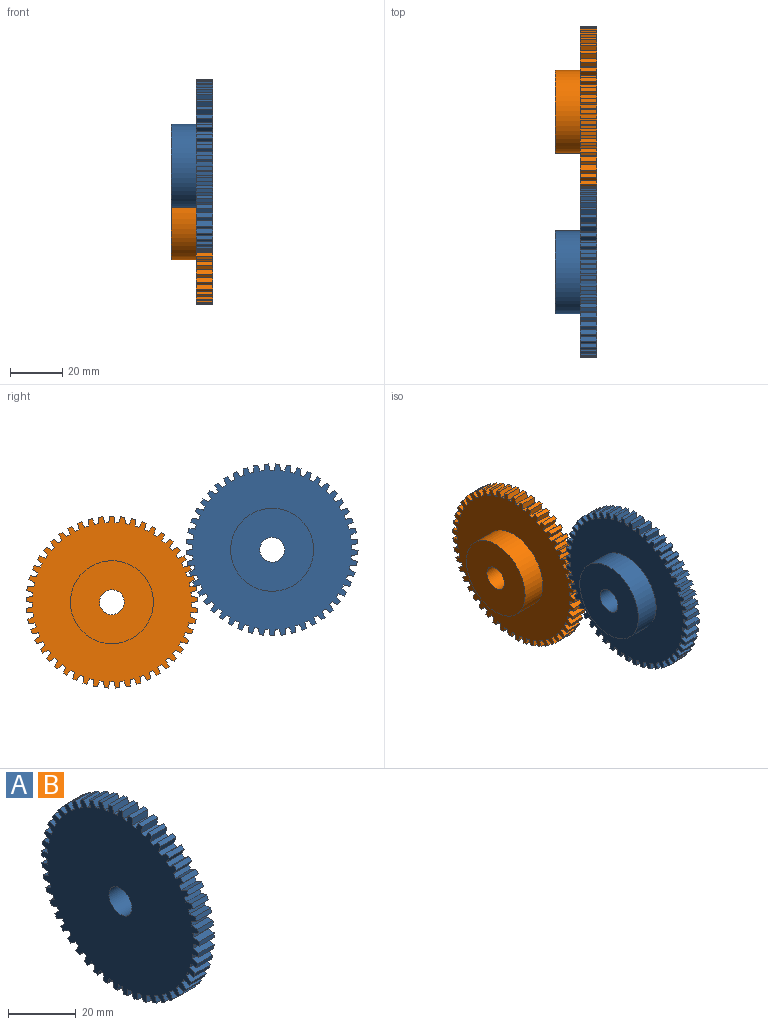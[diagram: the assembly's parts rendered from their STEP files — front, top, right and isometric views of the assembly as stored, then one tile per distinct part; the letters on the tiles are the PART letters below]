
ASSEMBLY  parts=2 mates=1
PART A: 201 faces, bbox 15.9x65.7x65.7 mm
  f0: cylinder r=30.48mm len=6.35mm, axis (-1,0,0), area 9.7mm2, adj f50,f51,f131,f134
  f1: cylinder r=30.48mm len=6.35mm, axis (-1,0,0), area 9.7mm2, adj f50,f51,f133,f137
  f2: cylinder r=30.48mm len=6.35mm, axis (-1,0,0), area 9.7mm2, adj f50,f51,f136,f140
  f3: cylinder r=30.48mm len=6.35mm, axis (-1,0,0), area 9.7mm2, adj f50,f51,f139,f143
  f4: cylinder r=30.48mm len=6.35mm, axis (-1,0,0), area 9.7mm2, adj f50,f51,f142,f146
  f5: cylinder r=30.48mm len=6.35mm, axis (-1,0,0), area 9.7mm2, adj f50,f51,f145,f149
  f6: cylinder r=30.48mm len=6.35mm, axis (-1,0,0), area 9.7mm2, adj f50,f51,f148,f152
  f7: cylinder r=30.48mm len=6.35mm, axis (-1,0,0), area 9.7mm2, adj f50,f51,f151,f155
  f8: cylinder r=30.48mm len=6.35mm, axis (-1,0,0), area 9.7mm2, adj f50,f51,f154,f158
  f9: cylinder r=30.48mm len=6.35mm, axis (-1,0,0), area 9.7mm2, adj f50,f51,f157,f161
  f10: cylinder r=30.48mm len=6.35mm, axis (-1,0,0), area 9.7mm2, adj f50,f51,f160,f164
  f11: cylinder r=30.48mm len=6.35mm, axis (-1,0,0), area 9.7mm2, adj f50,f51,f163,f167
  f12: cylinder r=30.48mm len=6.35mm, axis (-1,0,0), area 9.7mm2, adj f50,f51,f166,f170
  f13: cylinder r=30.48mm len=6.35mm, axis (-1,0,0), area 9.7mm2, adj f50,f51,f169,f173
  f14: cylinder r=30.48mm len=6.35mm, axis (-1,0,0), area 9.7mm2, adj f50,f51,f172,f176
  f15: cylinder r=30.48mm len=6.35mm, axis (-1,0,0), area 9.7mm2, adj f50,f51,f175,f179
  f16: cylinder r=30.48mm len=6.35mm, axis (-1,0,0), area 9.7mm2, adj f50,f51,f178,f182
  f17: cylinder r=30.48mm len=6.35mm, axis (-1,0,0), area 9.7mm2, adj f50,f51,f181,f185
  f18: cylinder r=30.48mm len=6.35mm, axis (-1,0,0), area 9.7mm2, adj f50,f51,f184,f188
  f19: cylinder r=30.48mm len=6.35mm, axis (-1,0,0), area 9.7mm2, adj f50,f51,f187,f191
  f20: cylinder r=30.48mm len=6.35mm, axis (-1,0,0), area 9.7mm2, adj f50,f51,f190,f194
  f21: cylinder r=30.48mm len=6.35mm, axis (-1,0,0), area 9.7mm2, adj f50,f51,f193,f197
  f22: cylinder r=30.48mm len=6.35mm, axis (-1,0,0), area 9.7mm2, adj f50,f51,f196,f198
  f23: cylinder r=30.48mm len=6.35mm, axis (-1,0,0), area 9.7mm2, adj f50,f51,f59,f200
  f24: cylinder r=30.48mm len=6.35mm, axis (-1,0,0), area 9.7mm2, adj f50,f51,f58,f62
  f25: cylinder r=30.48mm len=6.35mm, axis (-1,0,0), area 9.7mm2, adj f50,f51,f61,f65
  f26: cylinder r=30.48mm len=6.35mm, axis (-1,0,0), area 9.7mm2, adj f50,f51,f64,f68
  f27: cylinder r=30.48mm len=6.35mm, axis (-1,0,0), area 9.7mm2, adj f50,f51,f67,f71
  f28: cylinder r=30.48mm len=6.35mm, axis (-1,0,0), area 9.7mm2, adj f50,f51,f70,f74
  f29: cylinder r=30.48mm len=6.35mm, axis (-1,0,0), area 9.7mm2, adj f50,f51,f73,f77
  f30: cylinder r=30.48mm len=6.35mm, axis (-1,0,0), area 9.7mm2, adj f50,f51,f76,f80
  f31: cylinder r=30.48mm len=6.35mm, axis (-1,0,0), area 9.7mm2, adj f50,f51,f79,f83
  f32: cylinder r=30.48mm len=6.35mm, axis (-1,0,0), area 9.7mm2, adj f50,f51,f82,f86
  f33: cylinder r=30.48mm len=6.35mm, axis (-1,0,0), area 9.7mm2, adj f50,f51,f85,f89
  f34: cylinder r=30.48mm len=6.35mm, axis (-1,0,0), area 9.7mm2, adj f50,f51,f88,f92
  f35: cylinder r=30.48mm len=6.35mm, axis (-1,0,0), area 9.7mm2, adj f50,f51,f91,f95
  f36: cylinder r=30.48mm len=6.35mm, axis (-1,0,0), area 9.7mm2, adj f50,f51,f94,f98
  f37: cylinder r=30.48mm len=6.35mm, axis (-1,0,0), area 9.7mm2, adj f50,f51,f97,f101
  f38: cylinder r=30.48mm len=6.35mm, axis (-1,0,0), area 9.7mm2, adj f50,f51,f100,f104
  f39: cylinder r=30.48mm len=6.35mm, axis (-1,0,0), area 9.7mm2, adj f50,f51,f103,f107
  f40: cylinder r=30.48mm len=6.35mm, axis (-1,0,0), area 9.7mm2, adj f50,f51,f106,f110
  f41: cylinder r=30.48mm len=6.35mm, axis (-1,0,0), area 9.7mm2, adj f50,f51,f109,f113
  f42: cylinder r=30.48mm len=6.35mm, axis (-1,0,0), area 9.7mm2, adj f50,f51,f112,f116
  f43: cylinder r=30.48mm len=6.35mm, axis (-1,0,0), area 9.7mm2, adj f50,f51,f115,f119
  f44: cylinder r=30.48mm len=6.35mm, axis (-1,0,0), area 9.7mm2, adj f50,f51,f118,f122
  f45: cylinder r=30.48mm len=6.35mm, axis (-1,0,0), area 9.7mm2, adj f50,f51,f121,f125
  f46: cylinder r=30.48mm len=6.35mm, axis (-1,0,0), area 9.7mm2, adj f50,f51,f124,f128
  f47: cylinder r=30.48mm len=6.35mm, axis (-1,0,0), area 9.7mm2, adj f50,f51,f54,f127
  f48: cylinder r=30.48mm len=6.35mm, axis (-1,0,0), area 9.7mm2, adj f50,f51,f56,f130
  f49: cylinder r=15.88mm len=31.75mm, axis (-1,0,0), area 956.4mm2, adj f50,f53
  f50: plane 65.72x65.69mm, normal (1,0,0), area 2358mm2, adj f0,f1,f2,f3,f4,f5,f6,f7
  f51: plane 65.72x65.69mm, normal (-1,0,0), area 3078.4mm2, adj f0,f1,f2,f3,f4,f5,f6,f7
  f52: cylinder r=4.76mm len=15.94mm, axis (-1,0,0), area 476.9mm2, adj f51,f53
  f53: plane 31.75x31.75mm, normal (1,0,0), area 720.5mm2, adj f49,f52
  f54: plane 6.35x2.4mm, normal (0,-0.99,0.16), area 15.4mm2, adj f47,f50,f51,f55
  f55: plane 6.35x1.59mm, normal (0,0,1), area 10.1mm2, adj f50,f51,f54,f56
  f56: plane 6.35x2.4mm, normal (0,0.99,0.16), area 15.4mm2, adj f48,f50,f51,f55
  f57: plane 6.35x1.58mm, normal (0,-0.06,-1), area 10.1mm2, adj f50,f51,f58,f59
  f58: plane 6.35x2.42mm, normal (0,-0.99,-0.1), area 15.4mm2, adj f24,f50,f51,f57
  f59: plane 6.35x2.36mm, normal (0,0.97,-0.23), area 15.4mm2, adj f23,f50,f51,f57
  f60: plane 6.35x1.56mm, normal (0,-0.19,-0.98), area 10.1mm2, adj f50,f51,f61,f62
  f61: plane 6.35x2.43mm, normal (0,-1,0.03), area 15.4mm2, adj f25,f50,f51,f60
  f62: plane 6.35x2.28mm, normal (0,0.94,-0.35), area 15.4mm2, adj f24,f50,f51,f60
  f63: plane 6.35x1.51mm, normal (0,-0.32,-0.95), area 10.1mm2, adj f50,f51,f64,f65
  f64: plane 6.35x2.4mm, normal (0,-0.99,0.16), area 15.4mm2, adj f26,f50,f51,f63
  f65: plane 6.35x2.15mm, normal (0,0.88,-0.47), area 15.4mm2, adj f25,f50,f51,f63
  f66: plane 6.35x1.43mm, normal (0,-0.43,-0.9), area 10.1mm2, adj f50,f51,f67,f68
  f67: plane 6.35x2.33mm, normal (0,-0.96,0.28), area 15.4mm2, adj f27,f50,f51,f66
  f68: plane 6.35x1.99mm, normal (0,0.82,-0.58), area 15.4mm2, adj f26,f50,f51,f66
  f69: plane 6.35x1.33mm, normal (0,-0.55,-0.84), area 10.1mm2, adj f50,f51,f70,f71
  f70: plane 6.35x2.22mm, normal (0,-0.92,0.4), area 15.4mm2, adj f28,f50,f51,f69
  f71: plane 6.35x1.79mm, normal (0,0.74,-0.68), area 15.4mm2, adj f27,f50,f51,f69
  f72: plane 6.35x1.21mm, normal (0,-0.65,-0.76), area 10.1mm2, adj f50,f51,f73,f74
  f73: plane 6.35x2.08mm, normal (0,-0.86,0.52), area 15.4mm2, adj f29,f50,f51,f72
  f74: plane 6.35x1.85mm, normal (0,0.65,-0.76), area 15.4mm2, adj f28,f50,f51,f72
  f75: plane 6.35x1.18mm, normal (0,-0.74,-0.67), area 10.1mm2, adj f50,f51,f76,f77
  f76: plane 6.35x1.9mm, normal (0,-0.78,0.62), area 15.4mm2, adj f30,f50,f51,f75
  f77: plane 6.35x2.04mm, normal (0,0.54,-0.84), area 15.4mm2, adj f29,f50,f51,f75
  f78: plane 6.35x1.3mm, normal (0,-0.82,-0.57), area 10.1mm2, adj f50,f51,f79,f80
  f79: plane 6.35x1.74mm, normal (0,-0.7,0.72), area 15.4mm2, adj f31,f50,f51,f78
  f80: plane 6.35x2.19mm, normal (0,0.43,-0.9), area 15.4mm2, adj f30,f50,f51,f78
  f81: plane 6.35x1.41mm, normal (0,-0.89,-0.46), area 10.1mm2, adj f50,f51,f82,f83
  f82: plane 6.35x1.94mm, normal (0,-0.6,0.8), area 15.4mm2, adj f32,f50,f51,f81
  f83: plane 6.35x2.31mm, normal (0,0.31,-0.95), area 15.4mm2, adj f31,f50,f51,f81
  f84: plane 6.35x1.49mm, normal (0,-0.94,-0.35), area 10.1mm2, adj f50,f51,f85,f86
  f85: plane 6.35x2.11mm, normal (0,-0.49,0.87), area 15.4mm2, adj f33,f50,f51,f84
  f86: plane 6.35x2.38mm, normal (0,0.19,-0.98), area 15.4mm2, adj f32,f50,f51,f84
  f87: plane 6.35x1.55mm, normal (0,-0.97,-0.22), area 10.1mm2, adj f50,f51,f88,f89
  f88: plane 6.35x2.25mm, normal (0,-0.38,0.93), area 15.4mm2, adj f34,f50,f51,f87
  f89: plane 6.35x2.42mm, normal (0,0.06,-1), area 15.4mm2, adj f33,f50,f51,f87
  f90: plane 6.35x1.58mm, normal (0,-1,-0.1), area 10.1mm2, adj f50,f51,f91,f92
  f91: plane 6.35x2.35mm, normal (0,-0.26,0.97), area 15.4mm2, adj f35,f50,f51,f90
  f92: plane 6.35x2.42mm, normal (0,-0.07,-1), area 15.4mm2, adj f34,f50,f51,f90
  f93: plane 6.35x1.59mm, normal (0,-1,0.03), area 10.1mm2, adj f50,f51,f94,f95
  f94: plane 6.35x2.41mm, normal (0,-0.13,0.99), area 15.4mm2, adj f36,f50,f51,f93
  f95: plane 6.35x2.38mm, normal (0,-0.2,-0.98), area 15.4mm2, adj f35,f50,f51,f93
  f96: plane 6.35x1.57mm, normal (0,-0.99,0.16), area 10.1mm2, adj f50,f51,f97,f98
  f97: plane 6.35x2.43mm, normal (0,0,1), area 15.4mm2, adj f37,f50,f51,f96
  f98: plane 6.35x2.3mm, normal (0,-0.32,-0.95), area 15.4mm2, adj f36,f50,f51,f96
  f99: plane 6.35x1.52mm, normal (0,-0.96,0.28), area 10.1mm2, adj f50,f51,f100,f101
  f100: plane 6.35x2.41mm, normal (0,0.12,0.99), area 15.4mm2, adj f38,f50,f51,f99
  f101: plane 6.35x2.18mm, normal (0,-0.44,-0.9), area 15.4mm2, adj f37,f50,f51,f99
  f102: plane 6.35x1.45mm, normal (0,-0.91,0.4), area 10.1mm2, adj f50,f51,f103,f104
  f103: plane 6.35x2.35mm, normal (0,0.25,0.97), area 15.4mm2, adj f39,f50,f51,f102
  f104: plane 6.35x2.03mm, normal (0,-0.55,-0.84), area 15.4mm2, adj f38,f50,f51,f102
  f105: plane 6.35x1.36mm, normal (0,-0.86,0.52), area 10.1mm2, adj f50,f51,f106,f107
  f106: plane 6.35x2.25mm, normal (0,0.37,0.93), area 15.4mm2, adj f40,f50,f51,f105
  f107: plane 6.35x1.84mm, normal (0,-0.65,-0.76), area 15.4mm2, adj f39,f50,f51,f105
  f108: plane 6.35x1.24mm, normal (0,-0.78,0.62), area 10.1mm2, adj f50,f51,f109,f110
  f109: plane 6.35x2.12mm, normal (0,0.49,0.87), area 15.4mm2, adj f41,f50,f51,f108
  f110: plane 6.35x1.8mm, normal (0,-0.74,-0.67), area 15.4mm2, adj f40,f50,f51,f108
  f111: plane 6.35x1.14mm, normal (0,-0.7,0.72), area 10.1mm2, adj f50,f51,f112,f113
  f112: plane 6.35x1.95mm, normal (0,0.59,0.8), area 15.4mm2, adj f42,f50,f51,f111
  f113: plane 6.35x2mm, normal (0,-0.82,-0.57), area 15.4mm2, adj f41,f50,f51,f111
  f114: plane 6.35x1.27mm, normal (0,-0.6,0.8), area 10.1mm2, adj f50,f51,f115,f116
  f115: plane 6.35x1.75mm, normal (0,0.69,0.72), area 15.4mm2, adj f43,f50,f51,f114
  f116: plane 6.35x2.16mm, normal (0,-0.89,-0.46), area 15.4mm2, adj f42,f50,f51,f114
  f117: plane 6.35x1.38mm, normal (0,-0.49,0.87), area 10.1mm2, adj f50,f51,f118,f119
  f118: plane 6.35x1.89mm, normal (0,0.78,0.63), area 15.4mm2, adj f44,f50,f51,f117
  f119: plane 6.35x2.28mm, normal (0,-0.94,-0.34), area 15.4mm2, adj f43,f50,f51,f117
  f120: plane 6.35x1.47mm, normal (0,-0.38,0.93), area 10.1mm2, adj f50,f51,f121,f122
  f121: plane 6.35x2.07mm, normal (0,0.85,0.52), area 15.4mm2, adj f45,f50,f51,f120
  f122: plane 6.35x2.37mm, normal (0,-0.98,-0.22), area 15.4mm2, adj f44,f50,f51,f120
  f123: plane 6.35x1.54mm, normal (0,-0.25,0.97), area 10.1mm2, adj f50,f51,f124,f125
  f124: plane 6.35x2.22mm, normal (0,0.91,0.41), area 15.4mm2, adj f46,f50,f51,f123
  f125: plane 6.35x2.42mm, normal (0,-1,-0.09), area 15.4mm2, adj f45,f50,f51,f123
  f126: plane 6.35x1.57mm, normal (0,-0.13,0.99), area 10.1mm2, adj f50,f51,f127,f128
  f127: plane 6.35x2.32mm, normal (0,0.96,0.29), area 15.4mm2, adj f47,f50,f51,f126
  f128: plane 6.35x2.43mm, normal (0,-1,0.04), area 15.4mm2, adj f46,f50,f51,f126
  f129: plane 6.35x1.57mm, normal (0,0.13,0.99), area 10.1mm2, adj f50,f51,f130,f131
  f130: plane 6.35x2.32mm, normal (0,-0.96,0.29), area 15.4mm2, adj f48,f50,f51,f129
  f131: plane 6.35x2.43mm, normal (0,1,0.04), area 15.4mm2, adj f0,f50,f51,f129
  f132: plane 6.35x1.54mm, normal (0,0.25,0.97), area 10.1mm2, adj f50,f51,f133,f134
  f133: plane 6.35x2.42mm, normal (0,1,-0.09), area 15.4mm2, adj f1,f50,f51,f132
  f134: plane 6.35x2.22mm, normal (0,-0.91,0.41), area 15.4mm2, adj f0,f50,f51,f132
  f135: plane 6.35x1.47mm, normal (0,0.38,0.93), area 10.1mm2, adj f50,f51,f136,f137
  f136: plane 6.35x2.37mm, normal (0,0.98,-0.22), area 15.4mm2, adj f2,f50,f51,f135
  f137: plane 6.35x2.07mm, normal (0,-0.85,0.52), area 15.4mm2, adj f1,f50,f51,f135
  f138: plane 6.35x1.38mm, normal (0,0.49,0.87), area 10.1mm2, adj f50,f51,f139,f140
  f139: plane 6.35x2.28mm, normal (0,0.94,-0.34), area 15.4mm2, adj f3,f50,f51,f138
  f140: plane 6.35x1.89mm, normal (0,-0.78,0.63), area 15.4mm2, adj f2,f50,f51,f138
  f141: plane 6.35x1.27mm, normal (0,0.6,0.8), area 10.1mm2, adj f50,f51,f142,f143
  f142: plane 6.35x2.16mm, normal (0,0.89,-0.46), area 15.4mm2, adj f4,f50,f51,f141
  f143: plane 6.35x1.75mm, normal (0,-0.69,0.72), area 15.4mm2, adj f3,f50,f51,f141
  f144: plane 6.35x1.14mm, normal (0,0.7,0.72), area 10.1mm2, adj f50,f51,f145,f146
  f145: plane 6.35x2mm, normal (0,0.82,-0.57), area 15.4mm2, adj f5,f50,f51,f144
  f146: plane 6.35x1.95mm, normal (0,-0.59,0.8), area 15.4mm2, adj f4,f50,f51,f144
  f147: plane 6.35x1.24mm, normal (0,0.78,0.62), area 10.1mm2, adj f50,f51,f148,f149
  f148: plane 6.35x1.8mm, normal (0,0.74,-0.67), area 15.4mm2, adj f6,f50,f51,f147
  f149: plane 6.35x2.12mm, normal (0,-0.49,0.87), area 15.4mm2, adj f5,f50,f51,f147
  f150: plane 6.35x1.36mm, normal (0,0.86,0.52), area 10.1mm2, adj f50,f51,f151,f152
  f151: plane 6.35x1.84mm, normal (0,0.65,-0.76), area 15.4mm2, adj f7,f50,f51,f150
  f152: plane 6.35x2.25mm, normal (0,-0.37,0.93), area 15.4mm2, adj f6,f50,f51,f150
  f153: plane 6.35x1.45mm, normal (0,0.91,0.4), area 10.1mm2, adj f50,f51,f154,f155
  f154: plane 6.35x2.03mm, normal (0,0.55,-0.84), area 15.4mm2, adj f8,f50,f51,f153
  f155: plane 6.35x2.35mm, normal (0,-0.25,0.97), area 15.4mm2, adj f7,f50,f51,f153
  f156: plane 6.35x1.52mm, normal (0,0.96,0.28), area 10.1mm2, adj f50,f51,f157,f158
  f157: plane 6.35x2.18mm, normal (0,0.44,-0.9), area 15.4mm2, adj f9,f50,f51,f156
  f158: plane 6.35x2.41mm, normal (0,-0.12,0.99), area 15.4mm2, adj f8,f50,f51,f156
  f159: plane 6.35x1.57mm, normal (0,0.99,0.16), area 10.1mm2, adj f50,f51,f160,f161
  f160: plane 6.35x2.3mm, normal (0,0.32,-0.95), area 15.4mm2, adj f10,f50,f51,f159
  f161: plane 6.35x2.43mm, normal (0,0,1), area 15.4mm2, adj f9,f50,f51,f159
  f162: plane 6.35x1.59mm, normal (0,1,0.03), area 10.1mm2, adj f50,f51,f163,f164
  f163: plane 6.35x2.38mm, normal (0,0.2,-0.98), area 15.4mm2, adj f11,f50,f51,f162
  f164: plane 6.35x2.41mm, normal (0,0.13,0.99), area 15.4mm2, adj f10,f50,f51,f162
  f165: plane 6.35x1.58mm, normal (0,1,-0.1), area 10.1mm2, adj f50,f51,f166,f167
  f166: plane 6.35x2.42mm, normal (0,0.07,-1), area 15.4mm2, adj f12,f50,f51,f165
  f167: plane 6.35x2.35mm, normal (0,0.26,0.97), area 15.4mm2, adj f11,f50,f51,f165
  f168: plane 6.35x1.55mm, normal (0,0.97,-0.22), area 10.1mm2, adj f50,f51,f169,f170
  f169: plane 6.35x2.42mm, normal (0,-0.06,-1), area 15.4mm2, adj f13,f50,f51,f168
  f170: plane 6.35x2.25mm, normal (0,0.38,0.93), area 15.4mm2, adj f12,f50,f51,f168
  f171: plane 6.35x1.49mm, normal (0,0.94,-0.35), area 10.1mm2, adj f50,f51,f172,f173
  f172: plane 6.35x2.38mm, normal (0,-0.19,-0.98), area 15.4mm2, adj f14,f50,f51,f171
  f173: plane 6.35x2.11mm, normal (0,0.49,0.87), area 15.4mm2, adj f13,f50,f51,f171
  f174: plane 6.35x1.41mm, normal (0,0.89,-0.46), area 10.1mm2, adj f50,f51,f175,f176
  f175: plane 6.35x2.31mm, normal (0,-0.31,-0.95), area 15.4mm2, adj f15,f50,f51,f174
  f176: plane 6.35x1.94mm, normal (0,0.6,0.8), area 15.4mm2, adj f14,f50,f51,f174
  f177: plane 6.35x1.3mm, normal (0,0.82,-0.57), area 10.1mm2, adj f50,f51,f178,f179
  f178: plane 6.35x2.19mm, normal (0,-0.43,-0.9), area 15.4mm2, adj f16,f50,f51,f177
  f179: plane 6.35x1.74mm, normal (0,0.7,0.72), area 15.4mm2, adj f15,f50,f51,f177
  f180: plane 6.35x1.18mm, normal (0,0.74,-0.67), area 10.1mm2, adj f50,f51,f181,f182
  f181: plane 6.35x2.04mm, normal (0,-0.54,-0.84), area 15.4mm2, adj f17,f50,f51,f180
  f182: plane 6.35x1.9mm, normal (0,0.78,0.62), area 15.4mm2, adj f16,f50,f51,f180
  f183: plane 6.35x1.21mm, normal (0,0.65,-0.76), area 10.1mm2, adj f50,f51,f184,f185
  f184: plane 6.35x1.85mm, normal (0,-0.65,-0.76), area 15.4mm2, adj f18,f50,f51,f183
  f185: plane 6.35x2.08mm, normal (0,0.86,0.52), area 15.4mm2, adj f17,f50,f51,f183
  f186: plane 6.35x1.33mm, normal (0,0.55,-0.84), area 10.1mm2, adj f50,f51,f187,f188
  f187: plane 6.35x1.79mm, normal (0,-0.74,-0.68), area 15.4mm2, adj f19,f50,f51,f186
  f188: plane 6.35x2.22mm, normal (0,0.92,0.4), area 15.4mm2, adj f18,f50,f51,f186
  f189: plane 6.35x1.43mm, normal (0,0.43,-0.9), area 10.1mm2, adj f50,f51,f190,f191
  f190: plane 6.35x1.99mm, normal (0,-0.82,-0.58), area 15.4mm2, adj f20,f50,f51,f189
  f191: plane 6.35x2.33mm, normal (0,0.96,0.28), area 15.4mm2, adj f19,f50,f51,f189
  f192: plane 6.35x1.51mm, normal (0,0.32,-0.95), area 10.1mm2, adj f50,f51,f193,f194
  f193: plane 6.35x2.15mm, normal (0,-0.88,-0.47), area 15.4mm2, adj f21,f50,f51,f192
  f194: plane 6.35x2.4mm, normal (0,0.99,0.16), area 15.4mm2, adj f20,f50,f51,f192
  f195: plane 6.35x1.56mm, normal (0,0.19,-0.98), area 10.1mm2, adj f50,f51,f196,f197
  f196: plane 6.35x2.28mm, normal (0,-0.94,-0.35), area 15.4mm2, adj f22,f50,f51,f195
  f197: plane 6.35x2.43mm, normal (0,1,0.03), area 15.4mm2, adj f21,f50,f51,f195
  f198: plane 6.35x2.42mm, normal (0,0.99,-0.1), area 15.4mm2, adj f22,f50,f51,f199
  f199: plane 6.35x1.58mm, normal (0,0.06,-1), area 10.1mm2, adj f50,f51,f198,f200
  f200: plane 6.35x2.36mm, normal (0,-0.97,-0.23), area 15.4mm2, adj f23,f50,f51,f199
PART B: same geometry as A
PLACE A rot(axis=(0,-0.52,-0.86),180deg) t=(-47.32,-77.91,26.57)mm
PLACE B rot(axis=(0,0.96,-0.28),180deg) t=(-47.32,-23.4,0.31)mm
MATE fastened B.f101 <-> A.f113  axis (0,0.12,0.99) through (-34.56,-52.07,14.41)mm
